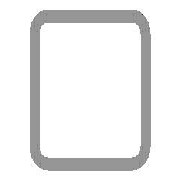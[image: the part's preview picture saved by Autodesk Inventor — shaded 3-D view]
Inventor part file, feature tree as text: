
AUTODESK INVENTOR PART (.ipt)
format: ipt  version: 2025 (Build 290162010, 162A)  size: 133,632 bytes
history: native  units: mm (DEFAULTED — no unit token found)
features: other x4, sketch x1, plane x1
ambient origin geometry x8: Origin, YZ Plane, XZ Plane, XY Plane, X Axis, Y Axis, Z Axis, Center Point
bodies: Solid1 (feature_tree), Body (feature_tree)
feature tree (6):
  parser-record x1  (decoder bookkeeping rows leaked as tree rows — omitted from the tree; the rows remain in map.json)
  other  "Driven Length"
  other  "Start Plane"
  other  "End Plane"
  sketch  "Sketch3"  dims[d3=2950.0mm d4=0.0mm d7=6.0mm d9=100.0mm d11=100.0mm d12=3.0mm d13=-0.0mm d14=2950.0mm d15=50.0mm d16=50.0mm d17=90.0deg d18=2950.0mm]
  plane  "Work Plane3"
